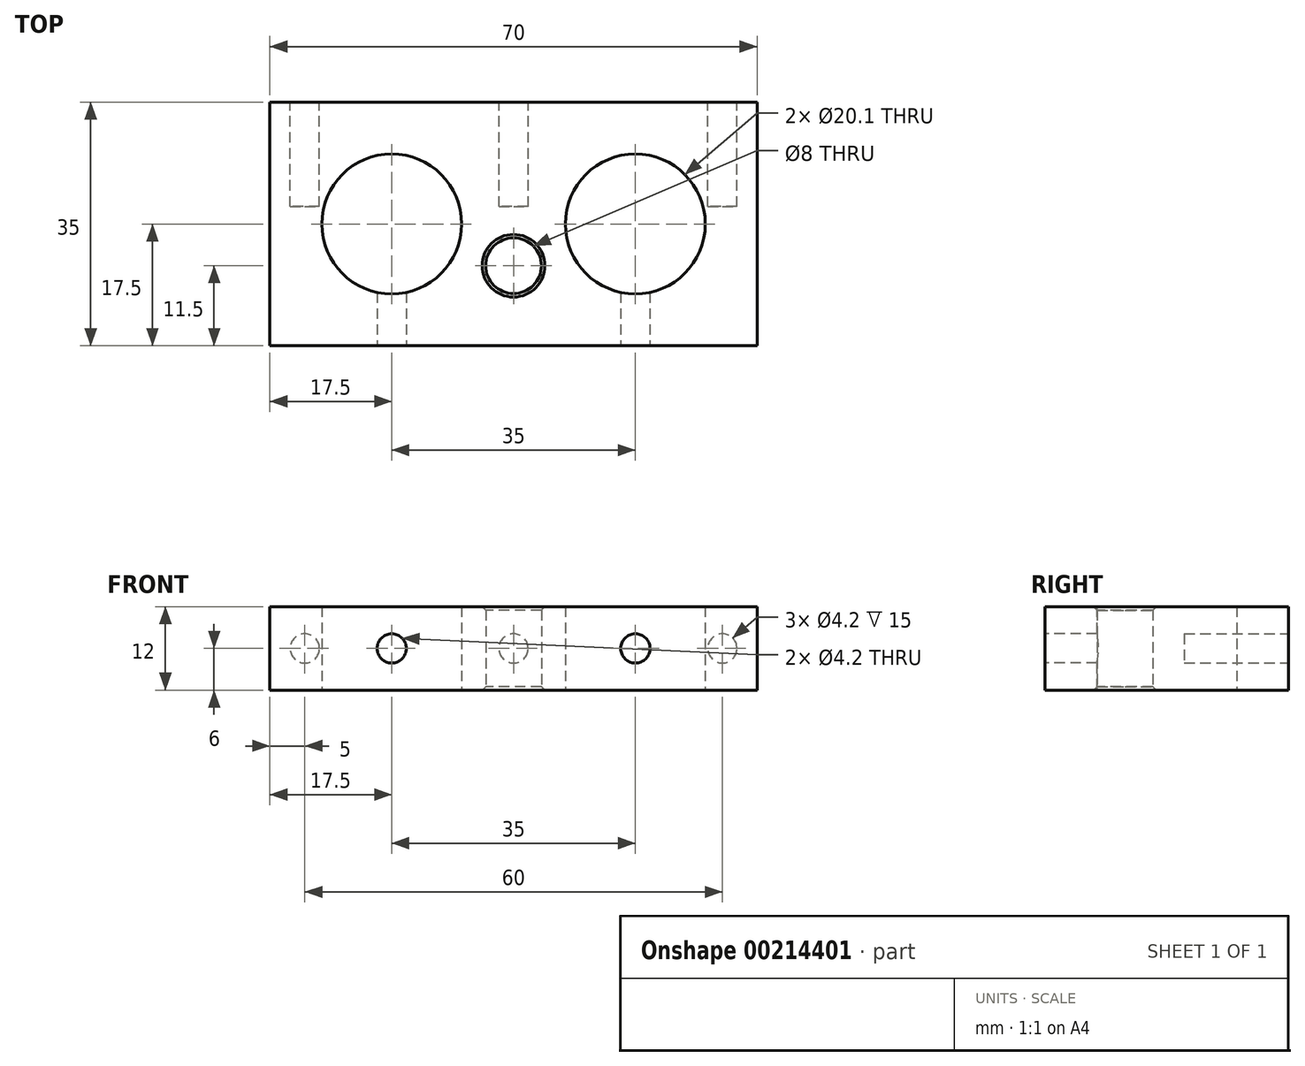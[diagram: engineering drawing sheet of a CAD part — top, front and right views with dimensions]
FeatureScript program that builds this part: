
annotation { "Feature Type Name" : "Feature", "Feature Type Description" : "" }
export const myFeature = defineFeature(function(context is Context, id is Id, definition is map)
    precondition{}
    {
        {
            var Q0;
            Q0=qCreatedBy(makeId("Top.planeOp"),FACE);
            var sketch = newSketch(context, id + "F0", { "sketchPlane" : qUnion([Q0])});
            skLineSegment(sketch, "E0.bottom", {"start": v(0, 0) * mm, "end": v(70, 0) * mm});
            skLineSegment(sketch, "E0.top", {"start": v(0, 35) * mm, "end": v(70, 35) * mm});
            skLineSegment(sketch, "E0.left", {"start": v(0, 0) * mm, "end": v(0, 35) * mm});
            skLineSegment(sketch, "E0.right", {"start": v(70, 0) * mm, "end": v(70, 35) * mm});
            skCircle(sketch, "E1", {"center": v(17.5, 17.5) * mm, "radius": 10.05 * mm});
            skCircle(sketch, "E2", {"center": v(52.5, 17.5) * mm, "radius": 10.05 * mm});
            skLineSegment(sketch, "E3", {"start": v(17.5, 17.5) * mm, "end": v(52.5, 17.5) * mm, "construction": true});
            skLineSegment(sketch, "E4", {"start": v(35, 35) * mm, "end": v(35, 17.5) * mm, "construction": true});
            skLineSegment(sketch, "E5", {"start": v(35, 17.5) * mm, "end": v(35, 11.5) * mm, "construction": true});
            skCircle(sketch, "E6", {"center": v(35, 11.5) * mm, "radius": 4 * mm});
            skSolve(sketch);
        }
        {
            var Q0;
            Q0 = qSketchRegion(id + "F0", true);
            extrude(context, id + "F1", {"entities" : qUnion([Q0]), "depth" : 12 * mm});
        }
        {
            var Q0;
            Q0=makeQuery(id+"F1.opExtrude","SWEPT_FACE",FACE,{"disambiguationData":[OSD([sQuery(id+"F0.wireOp",EDGE,"E0.top")])]});
            var sketch = newSketch(context, id + "F2", { "sketchPlane" : qUnion([Q0])});
            skLineSegment(sketch, "E7", {"start": v(0, 6) * mm, "end": v(-70, 6) * mm, "construction": true});
            skCircle(sketch, "E8", {"center": v(-35, 6) * mm, "radius": 2.1 * mm});
            skCircle(sketch, "E9", {"center": v(-65, 6) * mm, "radius": 2.1 * mm});
            skCircle(sketch, "E10", {"center": v(-5, 6) * mm, "radius": 2.1 * mm});
            skSolve(sketch);
        }
        {
            var Q0;
            Q0 = qSketchRegion(id + "F2", true);
            extrude(context, id + "F3", {"entities" : qUnion([Q0]), "operationType" : NewBodyOperationType.REMOVE, "oppositeDirection" : true, "depth" : 15 * mm});
        }
        {
            var Q0;
            Q0=makeQuery(id+"F1.opExtrude","SWEPT_FACE",FACE,{"disambiguationData":[OSD([sQuery(id+"F0.wireOp",EDGE,"E0.bottom")])]});
            var sketch = newSketch(context, id + "F4", { "sketchPlane" : qUnion([Q0])});
            skLineSegment(sketch, "E11", {"start": v(0, 6) * mm, "end": v(70, 6) * mm, "construction": true});
            skCircle(sketch, "E12", {"center": v(17.5, 6) * mm, "radius": 2.1 * mm});
            skCircle(sketch, "E13", {"center": v(52.5, 6) * mm, "radius": 2.1 * mm});
            skSolve(sketch);
        }
        {
            var Q0;
            Q0 = qSketchRegion(id + "F4", true);
            extrude(context, id + "F5", {"entities" : qUnion([Q0]), "operationType" : NewBodyOperationType.REMOVE, "endBound" : BoundingType.UP_TO_NEXT, "oppositeDirection" : true, "depth" : 25 * mm});
        }
        {
            var Q0;
            Q0=makeQuery(id+"F1.opExtrude","CAP_EDGE",EDGE,{"disambiguationData":[OSD([sQuery(id+"F0.wireOp",EDGE,"E6")])],"isStart":false});
            var Q1;
            Q1=makeQuery(id+"F1.opExtrude","CAP_EDGE",EDGE,{"disambiguationData":[OSD([sQuery(id+"F0.wireOp",EDGE,"E6")])],"isStart":true});
            chamfer(context, id + "F6", {"entities" : qUnion([Q0, Q1]), "width" : 0.5 * mm, "tangentPropagation" : true});
        }
    });
